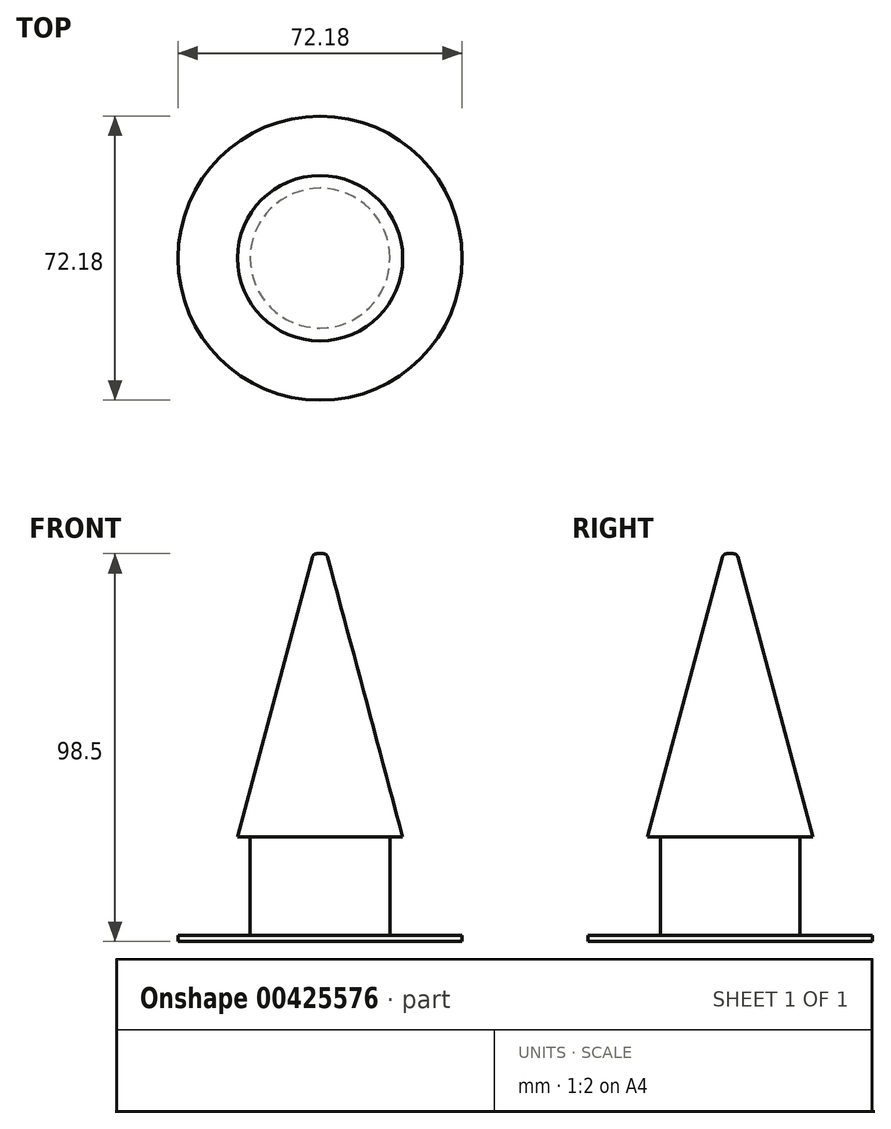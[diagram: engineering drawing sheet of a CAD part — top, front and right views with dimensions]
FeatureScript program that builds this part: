
annotation { "Feature Type Name" : "Feature", "Feature Type Description" : "" }
export const myFeature = defineFeature(function(context is Context, id is Id, definition is map)
    precondition{}
    {
        {
            var Q0;
            Q0=qCreatedBy(makeId("Top.planeOp"),FACE);
            var sketch = newSketch(context, id + "F0", { "sketchPlane" : qUnion([Q0])});
            skCircle(sketch, "E0", {"center": v(0, 0) * mm, "radius": 21 * mm});
            skSolve(sketch);
        }
        {
            var Q0;
            Q0=makeQuery(id+"F0.imprint","IMPRINT",FACE,{"disambiguationData":[TD([[makeQuery(id+"F0.imprint","IMPRINT",EDGE,{"derivedFrom":sQuery(id+"F0.wireOp",EDGE,"E0")}),1.0]])]});
            extrude(context, id + "F1", {"entities" : qUnion([Q0]), "depth" : 72 * mm, "hasDraft" : true, "draftAngle" : 15 * degree, "draftPullDirection" : true});
        }
        {
            var Q0;
            Q0=makeQuery(id+"F1.opExtrude","CAP_EDGE",EDGE,{"disambiguationData":[OSD([sQuery(id+"F0.wireOp",EDGE,"E0")])],"isStart":false});
            fillet(context, id + "F2", {"entities" : qUnion([Q0]), "radius" : 1.15 * mm, "tangentPropagation" : true, "rho" : 0.5, "crossSection" : FilletCrossSection.CONIC, "allowEdgeOverflow" : false});
        }
        {
            var Q0;
            Q0=makeQuery(id+"F1.opExtrude","CAP_FACE",FACE,{"disambiguationData":[OSD([sQuery(id+"F0.wireOp",EDGE,"E0")])],"isStart":true});
            var sketch = newSketch(context, id + "F3", { "sketchPlane" : qUnion([Q0])});
            skCircle(sketch, "E1", {"center": v(0, 0) * mm, "radius": 17.75 * mm});
            skSolve(sketch);
        }
        {
            var Q0;
            Q0=makeQuery(id+"F3.imprint","IMPRINT",FACE,{"disambiguationData":[TD([[makeQuery(id+"F3.imprint","IMPRINT",EDGE,{"derivedFrom":sQuery(id+"F3.wireOp",EDGE,"E1")}),1.0]])]});
            extrude(context, id + "F4", {"entities" : qUnion([Q0]), "operationType" : NewBodyOperationType.ADD, "depth" : 25 * mm});
        }
        {
            var Q0;
            Q0=makeQuery(id+"F4.opExtrude","CAP_FACE",FACE,{"disambiguationData":[OSD([sQuery(id+"F3.wireOp",EDGE,"E1")])],"isStart":false});
            var sketch = newSketch(context, id + "F5", { "sketchPlane" : qUnion([Q0])});
            skCircle(sketch, "E2", {"center": v(0, 0) * mm, "radius": 36.09 * mm});
            skSolve(sketch);
        }
        {
            var Q0;
            Q0 = qSketchRegion(id + "F5", true);
            extrude(context, id + "F6", {"entities" : qUnion([Q0]), "operationType" : NewBodyOperationType.ADD, "depth" : 1.5 * mm});
        }
    });
